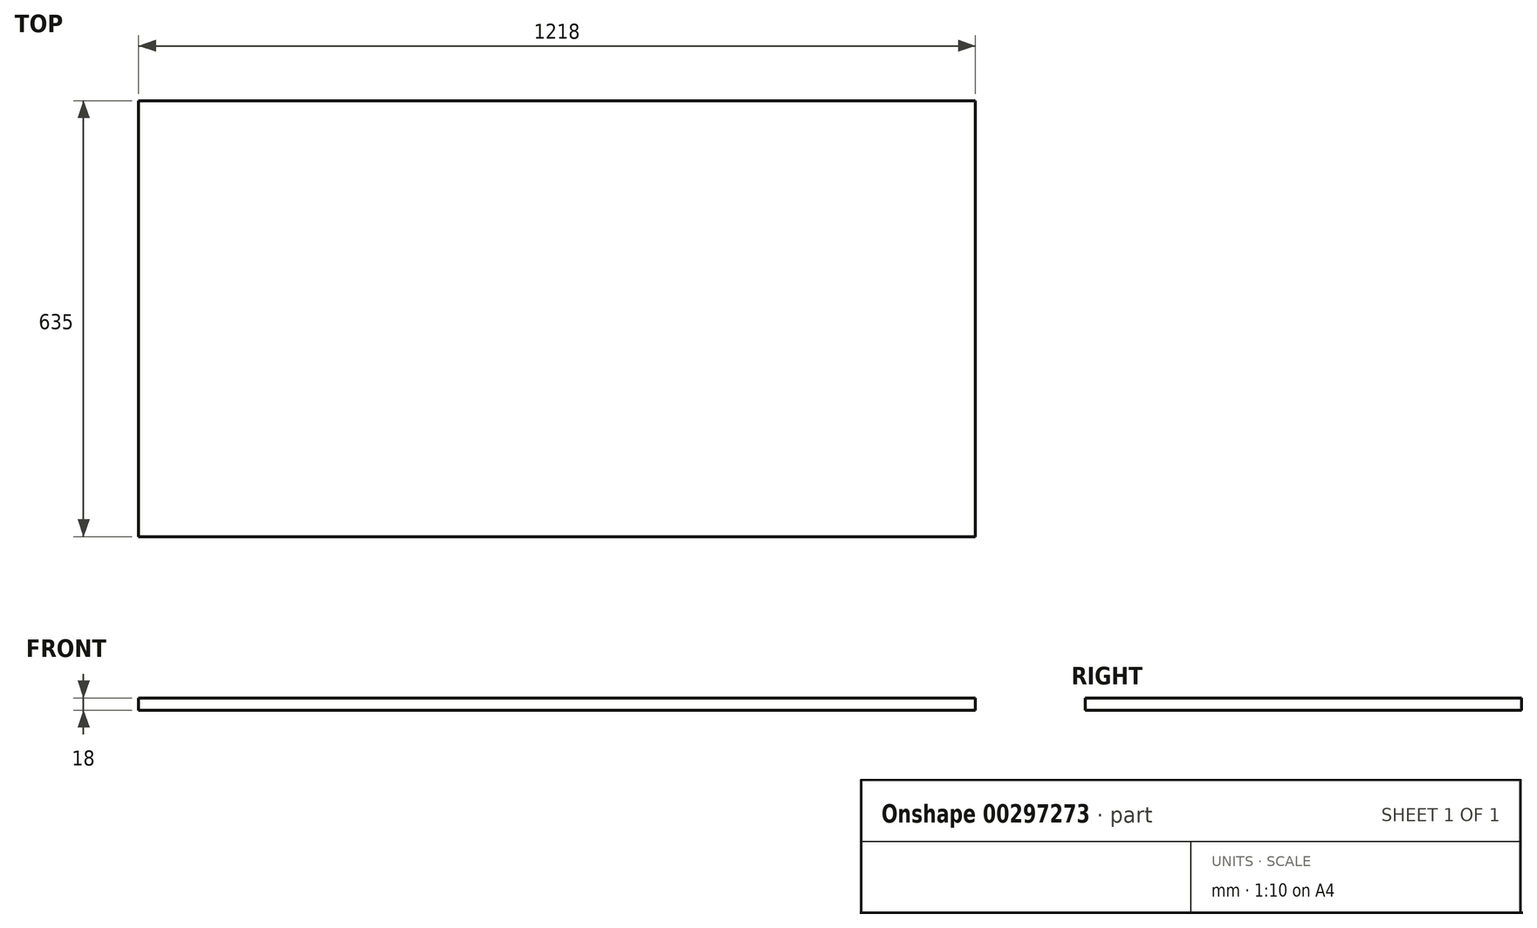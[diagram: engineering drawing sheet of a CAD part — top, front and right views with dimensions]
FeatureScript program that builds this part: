
annotation { "Feature Type Name" : "Feature", "Feature Type Description" : "" }
export const myFeature = defineFeature(function(context is Context, id is Id, definition is map)
    precondition{}
    {
        {
            var Q0;
            Q0=qCreatedBy(makeId("Top.planeOp"),FACE);
            var sketch = newSketch(context, id + "F0", { "sketchPlane" : qUnion([Q0])});
            skLineSegment(sketch, "E0.bottom", {"start": v(609, -317.5) * mm, "end": v(-609, -317.5) * mm});
            skLineSegment(sketch, "E0.top", {"start": v(609, 317.5) * mm, "end": v(-609, 317.5) * mm});
            skLineSegment(sketch, "E0.left", {"start": v(609, -317.5) * mm, "end": v(609, 317.5) * mm});
            skLineSegment(sketch, "E0.right", {"start": v(-609, -317.5) * mm, "end": v(-609, 317.5) * mm});
            skPoint(sketch, "E0.middle", {"position": v(0, 0) * mm});
            skSolve(sketch);
        }
        {
            var Q0;
            Q0 = qSketchRegion(id + "F0", true);
            extrude(context, id + "F1", {"entities" : qUnion([Q0]), "depth" : 18 * mm});
        }
    });
